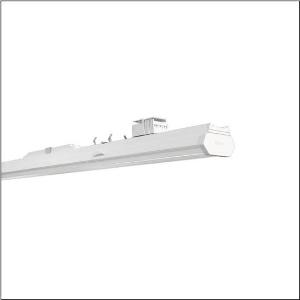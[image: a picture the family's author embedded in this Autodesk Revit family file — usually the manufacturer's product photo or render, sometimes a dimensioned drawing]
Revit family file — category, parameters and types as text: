
# Revit family: licross_r__21_protected_mo_52td1bmn4axg_a5a6
name_source: partatom
category: Lighting Fixtures
units: mm (PartAtom-declared; Revit-internal decimal feet)

## family parameters
Cut with Voids When Loaded = No
Host = Face
Light Source = No
Part Type = Normal
Room Calculation Point = No
Round Connector Dimension = Use Diameter
Shared = No

## types (1)
- --- (1 x LED, 10100 lm, 60.5 W, 4000K)
    Apparent Load = 61 VA
    CIE Flux Codes = 54 82 95 97 100
    Color Rendering = 80
    Color Temperature = 4000K
    Default Elevation = 1800 mm
    Description = Licross® 21 Protected MO, luminaire insert, of sheet steel, galvanised, coil coated, white, length: 1.500mm, width: 90mm, height: 103mm, LED rated luminous flux: 10.100lm, light colour: 840, control gear: ON/OFF Multilumen, with plug, 3-pole, with phase selection, mains connection: 220..240V, AC, 50/60Hz, rated input power: 61W, halogen-free wiring, primary optical cover: cover, of PMMA, light emission: direct distribution, primary light characteristic: symmetric, protection rating (complete): IP54, insulation class (complete): insulation class I (protective earthing), certification: CE, ENEC, VDE, UKCA, protection symbol: D if used in an environment with non-conductive dust loads with corresponding accessories, impact resistance: IK06, permissible ambient temperature for indoor applications: -35..+45°C, corresponds to IFS (International Featured Standards) requirements for safety and quality in the food industry, reducing of maximum allowable ambient temperature of 5°C with ceiling mounting, LABS conformity tested according to VDMA 24364:2018-05, packaging unit: 1 piece
    Height = 92 mm
    Lamp = 1 x LED
    Lamp Light Flux = 10100 lm
    Lamp Power = 60.5 W
    Lamp count = 1
    Length = 1500 mm
    Luminous efficacy = 167 lm/W
    Manufacturer = Siteco
    ModVariant = No
    Model = 52TD1BMN4AXG
    Mounting Place = Ceiling
    Mounting Type = Pendant
    Number of Poles = 1
    OnlyDefault = Yes
    Power Factor = 1
    Product Name = Licross® 21 Protected MO
    Product group = luminaire insert
    ProductGroupID = 901
    Protection Class = Protection class I
    Protection Degree = IP 54
    RLX_Detail_Level = 1
    RLX_Emergency_Light_Flux = 0 lm
    RLX_Emergency_Type = 0
    RLX_Emergency_Type_DB = No
    RlxData = <blob elided: 22121 chars, md5=47bffec2>
    Socket = socket
    Standby Power = 0 W
    System Light Flux = 10100 lm
    System Power = 61 W
    Type Comments = factory setting: luminous flux: 100 % | (A | C | E) | 140 mA
    Type Image = l_1256148.jpg
    URL = http://relux.com
    VarID = @adj_057477
    Voltage = 0 V
    Weight = 0.00 kg
    Width = 88 mm

## geometry (parser evidence)
native form markers: Blend x4, Sweep x11
no freeform markers — native parametric forms only
